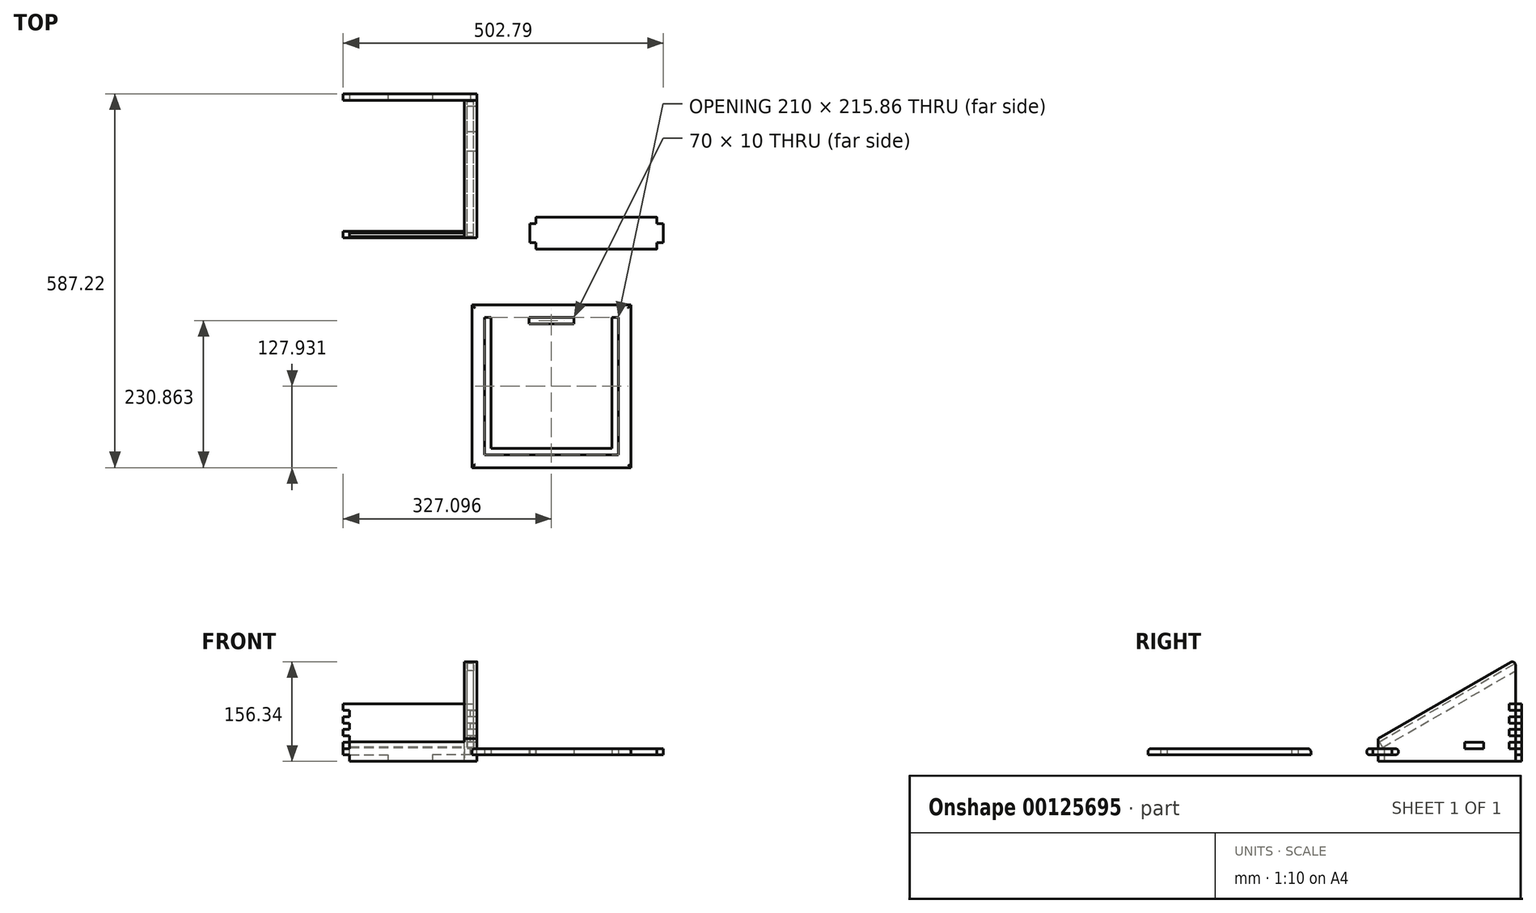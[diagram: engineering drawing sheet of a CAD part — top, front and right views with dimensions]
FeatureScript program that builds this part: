
annotation { "Feature Type Name" : "Feature", "Feature Type Description" : "" }
export const myFeature = defineFeature(function(context is Context, id is Id, definition is map)
    precondition{}
    {
        {
            var Q0;
            Q0=qCreatedBy(makeId("Right.planeOp"),FACE);
            var sketch = newSketch(context, id + "F0", { "sketchPlane" : qUnion([Q0])});
            skLineSegment(sketch, "E0", {"start": v(5, 25.39) * mm, "end": v(220.84, 150) * mm});
            skLineSegment(sketch, "E1", {"start": v(220.84, 150) * mm, "end": v(220.84, 80) * mm});
            skPoint(sketch, "E2.orphan", {"position": v(-38.97, 0) * mm});
            skLineSegment(sketch, "E3", {"start": v(-38.97, 0) * mm, "end": v(0, 22.5) * mm, "construction": true});
            skLineSegment(sketch, "E4", {"start": v(-38.97, 0) * mm, "end": v(0, 0) * mm, "construction": true});
            skLineSegment(sketch, "E5.top", {"start": v(5, -10) * mm, "end": v(220.84, -10) * mm});
            skLineSegment(sketch, "E5.right", {"start": v(220.84, 0) * mm, "end": v(220.84, -10) * mm});
            skLineSegment(sketch, "E6", {"start": v(210.84, -10) * mm, "end": v(210.84, 144.23) * mm, "construction": true});
            skLineSegment(sketch, "E7.bottom", {"start": v(220.84, 10) * mm, "end": v(210.84, 10) * mm});
            skLineSegment(sketch, "E7.top", {"start": v(220.84, 20) * mm, "end": v(210.84, 20) * mm});
            skLineSegment(sketch, "E7.right", {"start": v(210.84, 10) * mm, "end": v(210.84, 20) * mm});
            skLineSegment(sketch, "E8.bottom", {"start": v(220.84, 30) * mm, "end": v(210.84, 30) * mm});
            skLineSegment(sketch, "E8.top", {"start": v(220.84, 40) * mm, "end": v(210.84, 40) * mm});
            skLineSegment(sketch, "E8.right", {"start": v(210.84, 30) * mm, "end": v(210.84, 40) * mm});
            skLineSegment(sketch, "E9.bottom", {"start": v(220.84, 50) * mm, "end": v(210.84, 50) * mm});
            skLineSegment(sketch, "E9.top", {"start": v(220.84, 60) * mm, "end": v(210.84, 60) * mm});
            skLineSegment(sketch, "E9.right", {"start": v(210.84, 50) * mm, "end": v(210.84, 60) * mm});
            skLineSegment(sketch, "E10.trimOffspring", {"start": v(220.84, 10) * mm, "end": v(220.84, 0) * mm});
            skLineSegment(sketch, "E11.trimOffspring", {"start": v(220.84, 30) * mm, "end": v(220.84, 20) * mm});
            skLineSegment(sketch, "E12.trimOffspring", {"start": v(220.84, 50) * mm, "end": v(220.84, 40) * mm});
            skLineSegment(sketch, "E13", {"start": v(220.84, 70) * mm, "end": v(210.84, 70) * mm});
            skLineSegment(sketch, "E14", {"start": v(210.84, 70) * mm, "end": v(210.84, 80) * mm});
            skLineSegment(sketch, "E15", {"start": v(210.84, 80) * mm, "end": v(220.84, 80) * mm});
            skLineSegment(sketch, "E16.trimOffspring", {"start": v(220.84, 70) * mm, "end": v(220.84, 60) * mm});
            skLineSegment(sketch, "E17.bottom", {"start": v(170.84, 10) * mm, "end": v(140.84, 10) * mm});
            skLineSegment(sketch, "E17.top", {"start": v(170.84, 20) * mm, "end": v(140.84, 20) * mm});
            skLineSegment(sketch, "E17.left", {"start": v(170.84, 10) * mm, "end": v(170.84, 20) * mm});
            skLineSegment(sketch, "E17.right", {"start": v(140.84, 10) * mm, "end": v(140.84, 20) * mm});
            skLineSegment(sketch, "E18", {"start": v(5, -10) * mm, "end": v(5, 0) * mm});
            skLineSegment(sketch, "E19", {"start": v(0, 22.5) * mm, "end": v(5, 25.39) * mm, "construction": true});
            skLineSegment(sketch, "E20", {"start": v(5, -10) * mm, "end": v(0, -10) * mm, "construction": true});
            skLineSegment(sketch, "E21", {"start": v(0, -10) * mm, "end": v(0, 0) * mm, "construction": true});
            skLineSegment(sketch, "E22", {"start": v(0, 22.5) * mm, "end": v(0, 0) * mm, "construction": true});
            skLineSegment(sketch, "E23", {"start": v(5, 0) * mm, "end": v(15, 0) * mm});
            skLineSegment(sketch, "E24", {"start": v(15, 0) * mm, "end": v(15, 10) * mm});
            skLineSegment(sketch, "E25", {"start": v(15, 10) * mm, "end": v(5, 10) * mm});
            skLineSegment(sketch, "E26.trimOffspring", {"start": v(5, 10) * mm, "end": v(5, 25.39) * mm});
            skSolve(sketch);
        }
        {
            var Q0;
            Q0 = qSketchRegion(id + "F0", true);
            extrude(context, id + "F1", {"entities" : qUnion([Q0]), "depth" : 10 * mm});
        }
        {
            var Q0;
            Q0=makeQuery(id+"F1.opExtrude","SWEPT_EDGE",EDGE,{"disambiguationData":[OSD([sQuery(id+"F0.wireOp",EDGE,"E0"),sQuery(id+"F0.wireOp",EDGE,"E1")])]});
            cPlane(context, id + "F2", {"entities" : qUnion([Q0]), "cplaneType" : CPlaneType.LINE_ANGLE, "offset" : 25 * mm, "angle" : 330 * degree, "width" : 150 * mm, "height" : 150 * mm});
        }
        {
            var Q0;
            Q0=qCreatedBy(id+"F2.planeOp",FACE);
            var sketch = newSketch(context, id + "F3", { "sketchPlane" : qUnion([Q0])});
            skLineSegment(sketch, "E27.bottom", {"start": v(5, 14.49) * mm, "end": v(0, 14.49) * mm});
            skLineSegment(sketch, "E27.top", {"start": v(5, 3.99) * mm, "end": v(0, 3.99) * mm});
            skLineSegment(sketch, "E27.left", {"start": v(5, 14.49) * mm, "end": v(5, 3.99) * mm});
            skLineSegment(sketch, "E27.right", {"start": v(0, 14.49) * mm, "end": v(0, 3.99) * mm});
            skSolve(sketch);
        }
        {
            var Q0;
            Q0 = qSketchRegion(id + "F3", true);
            extrude(context, id + "F4", {"entities" : qUnion([Q0]), "operationType" : NewBodyOperationType.REMOVE, "depth" : 250 * mm});
        }
        {
            var Q0;
            Q0=makeQuery(id+"F1.opExtrude","SWEPT_BODY",BODY,{"disambiguationData":[OSD([sQuery(id+"F0.wireOp",EDGE,"E0"),sQuery(id+"F0.wireOp",EDGE,"E1"),sQuery(id+"F0.wireOp",EDGE,"fb4f92bf-d50f-4f46-b588-a990c1f543ed"),sQuery(id+"F0.wireOp",EDGE,"E5.top"),sQuery(id+"F0.wireOp",EDGE,"E5.left"),sQuery(id+"F0.wireOp",EDGE,"E5.right")])]});
            var Q1;
            Q1=qCreatedBy(makeId("Right.planeOp"),FACE);
            mirror(context, id + "F5", {"entities" : qUnion([Q0]), "mirrorPlane" : qUnion([Q1])});
        }
        {
            var Q0;
            Q0=qCreatedBy(makeId("Top.planeOp"),FACE);
            var sketch = newSketch(context, id + "F6", { "sketchPlane" : qUnion([Q0])});
            skLineSegment(sketch, "E28.bottom", {"start": v(2.1, -100.52) * mm, "end": v(252.1, -100.52) * mm});
            skLineSegment(sketch, "E28.top", {"start": v(2.1, -356.38) * mm, "end": v(252.1, -356.38) * mm});
            skLineSegment(sketch, "E28.left", {"start": v(2.1, -100.52) * mm, "end": v(2.1, -356.38) * mm});
            skLineSegment(sketch, "E28.right", {"start": v(252.1, -100.52) * mm, "end": v(252.1, -356.38) * mm});
            skLineSegment(sketch, "E29.0", {"start": v(232.1, -120.52) * mm, "end": v(232.1, -336.38) * mm});
            skLineSegment(sketch, "E29.2", {"start": v(22.1, -120.52) * mm, "end": v(22.1, -336.38) * mm});
            skLineSegment(sketch, "E30.0", {"start": v(222.1, -120.52) * mm, "end": v(222.1, -326.38) * mm});
            skLineSegment(sketch, "E30.2", {"start": v(32.1, -120.52) * mm, "end": v(32.1, -326.38) * mm});
            skLineSegment(sketch, "E31", {"start": v(22.1, -120.52) * mm, "end": v(32.1, -120.52) * mm});
            skLineSegment(sketch, "E32.trimOffspring", {"start": v(222.1, -120.52) * mm, "end": v(232.1, -120.52) * mm});
            skLineSegment(sketch, "E33.bottom", {"start": v(31.23, -336.38) * mm, "end": v(223, -336.38) * mm});
            skLineSegment(sketch, "E33.top", {"start": v(32.1, -326.38) * mm, "end": v(222.1, -326.38) * mm});
            skLineSegment(sketch, "E34.bottom", {"start": v(92.1, -120.52) * mm, "end": v(162.1, -120.52) * mm});
            skLineSegment(sketch, "E34.top", {"start": v(92.1, -130.52) * mm, "end": v(162.1, -130.52) * mm});
            skLineSegment(sketch, "E34.left", {"start": v(92.1, -120.52) * mm, "end": v(92.1, -130.52) * mm});
            skLineSegment(sketch, "E34.right", {"start": v(162.1, -120.52) * mm, "end": v(162.1, -130.52) * mm});
            skLineSegment(sketch, "E35", {"start": v(31.23, -336.38) * mm, "end": v(22.1, -336.38) * mm});
            skLineSegment(sketch, "E36", {"start": v(223, -336.38) * mm, "end": v(232.1, -336.38) * mm});
            skSolve(sketch);
        }
        {
            var Q0;
            Q0 = qSketchRegion(id + "F6", true);
            extrude(context, id + "F7", {"entities" : qUnion([Q0]), "depth" : 10 * mm});
        }
        {
            var Q0;
            Q0=makeQuery(id+"F1.opExtrude","CAP_FACE",FACE,{"disambiguationData":[OSD([sQuery(id+"F0.wireOp",EDGE,"E0"),sQuery(id+"F0.wireOp",EDGE,"E1"),sQuery(id+"F0.wireOp",EDGE,"fb4f92bf-d50f-4f46-b588-a990c1f543ed"),sQuery(id+"F0.wireOp",EDGE,"E5.top"),sQuery(id+"F0.wireOp",EDGE,"E5.left"),sQuery(id+"F0.wireOp",EDGE,"E5.right")])],"isStart":true});
            var sketch = newSketch(context, id + "F8", { "sketchPlane" : qUnion([Q0])});
            skLineSegment(sketch, "E37", {"start": v(-5, -10) * mm, "end": v(-15, -10) * mm});
            skLineSegment(sketch, "E38", {"start": v(-15, -10) * mm, "end": v(-15, 13.26) * mm});
            skLineSegment(sketch, "E39", {"start": v(-15, 13.26) * mm, "end": v(-12.08, 11.58) * mm});
            skLineSegment(sketch, "E40", {"start": v(-12.08, 11.58) * mm, "end": v(-6.83, 20.67) * mm});
            skLineSegment(sketch, "E41", {"start": v(-5, -10) * mm, "end": v(-5, 20.67) * mm});
            skLineSegment(sketch, "E42", {"start": v(-15, 13.26) * mm, "end": v(-15, 25.39) * mm, "construction": true});
            skLineSegment(sketch, "E43", {"start": v(-6.83, 20.67) * mm, "end": v(-5, 20.67) * mm});
            skSolve(sketch);
        }
        {
            var Q0;
            Q0 = qSketchRegion(id + "F8", true);
            extrude(context, id + "F9", {"entities" : qUnion([Q0]), "depth" : 190 * mm});
        }
        {
            var Q0;
            Q0=makeQuery(id+"F9.opExtrude","SWEPT_FACE",FACE,{"disambiguationData":[OSD([sQuery(id+"F8.wireOp",EDGE,"E41")])]});
            var sketch = newSketch(context, id + "F10", { "sketchPlane" : qUnion([Q0])});
            skLineSegment(sketch, "E44.bottom", {"start": v(0, 0) * mm, "end": v(10, 0) * mm});
            skLineSegment(sketch, "E44.top", {"start": v(0, 10) * mm, "end": v(10, 10) * mm});
            skLineSegment(sketch, "E44.left", {"start": v(0, 0) * mm, "end": v(0, 10) * mm});
            skLineSegment(sketch, "E44.right", {"start": v(10, 0) * mm, "end": v(10, 10) * mm});
            skLineSegment(sketch, "E45.bottom", {"start": v(-190, 0) * mm, "end": v(-200, 0) * mm});
            skLineSegment(sketch, "E45.top", {"start": v(-190, 10) * mm, "end": v(-200, 10) * mm});
            skLineSegment(sketch, "E45.left", {"start": v(-190, 0) * mm, "end": v(-190, 10) * mm});
            skLineSegment(sketch, "E45.right", {"start": v(-200, 0) * mm, "end": v(-200, 10) * mm});
            skSolve(sketch);
        }
        {
            var Q0;
            Q0 = qSketchRegion(id + "F10", true);
            extrude(context, id + "F11", {"entities" : qUnion([Q0]), "operationType" : NewBodyOperationType.ADD, "oppositeDirection" : true, "depth" : 10 * mm});
        }
        {
            var Q0;
            Q0=makeQuery(id+"F1.opExtrude","SWEPT_FACE",FACE,{"disambiguationData":[OSD([sQuery(id+"F0.wireOp",EDGE,"E5.right"),sQuery(id+"F0.wireOp",EDGE,"E10.trimOffspring")])]});
            var sketch = newSketch(context, id + "F12", { "sketchPlane" : qUnion([Q0])});
            skLineSegment(sketch, "E46", {"start": v(0, 0) * mm, "end": v(0, 10) * mm});
            skLineSegment(sketch, "E47", {"start": v(0, 10) * mm, "end": v(-10, 10) * mm});
            skLineSegment(sketch, "E48", {"start": v(-10, 10) * mm, "end": v(-10, 20) * mm});
            skLineSegment(sketch, "E49", {"start": v(-10, 20) * mm, "end": v(0, 20) * mm});
            skLineSegment(sketch, "E50", {"start": v(0, 20) * mm, "end": v(0, 30) * mm});
            skLineSegment(sketch, "E51", {"start": v(0, 30) * mm, "end": v(-10, 30) * mm});
            skLineSegment(sketch, "E52", {"start": v(-10, 30) * mm, "end": v(-10, 40) * mm});
            skLineSegment(sketch, "E53", {"start": v(-10, 40) * mm, "end": v(0, 40) * mm});
            skLineSegment(sketch, "E54", {"start": v(0, 40) * mm, "end": v(0, 50) * mm});
            skLineSegment(sketch, "E55", {"start": v(0, 50) * mm, "end": v(-10, 50) * mm});
            skLineSegment(sketch, "E56", {"start": v(-10, 50) * mm, "end": v(-10, 60) * mm});
            skLineSegment(sketch, "E57", {"start": v(-10, 60) * mm, "end": v(0, 60) * mm});
            skLineSegment(sketch, "E58", {"start": v(95, -10) * mm, "end": v(95, 115.91) * mm, "construction": true});
            skLineSegment(sketch, "E59", {"start": v(0, 0) * mm, "end": v(60, 0) * mm});
            skLineSegment(sketch, "E60", {"start": v(60, 0) * mm, "end": v(60, -10) * mm});
            skLineSegment(sketch, "E61", {"start": v(60, -10) * mm, "end": v(95, -10) * mm});
            skLineSegment(sketch, "E62.MirrorCS", {"start": v(190, 50) * mm, "end": v(200, 50) * mm});
            skLineSegment(sketch, "E63.MirrorCS", {"start": v(190, 40) * mm, "end": v(190, 50) * mm});
            skLineSegment(sketch, "E64.MirrorCS", {"start": v(200, 50) * mm, "end": v(200, 60) * mm});
            skLineSegment(sketch, "E65.MirrorCS", {"start": v(200, 40) * mm, "end": v(190, 40) * mm});
            skLineSegment(sketch, "E66.MirrorCS", {"start": v(200, 60) * mm, "end": v(190, 60) * mm});
            skLineSegment(sketch, "E67.MirrorCS", {"start": v(200, 30) * mm, "end": v(200, 40) * mm});
            skLineSegment(sketch, "E68.MirrorCS", {"start": v(190, 30) * mm, "end": v(200, 30) * mm});
            skLineSegment(sketch, "E69.MirrorCS", {"start": v(190, 20) * mm, "end": v(190, 30) * mm});
            skLineSegment(sketch, "E70.MirrorCS", {"start": v(200, 20) * mm, "end": v(190, 20) * mm});
            skLineSegment(sketch, "E71.MirrorCS", {"start": v(190, 10) * mm, "end": v(200, 10) * mm});
            skLineSegment(sketch, "E72.MirrorCS", {"start": v(200, 10) * mm, "end": v(200, 20) * mm});
            skLineSegment(sketch, "E73.MirrorCS", {"start": v(190, 0) * mm, "end": v(190, 10) * mm});
            skLineSegment(sketch, "E74.MirrorCS", {"start": v(190, 0) * mm, "end": v(130, 0) * mm});
            skLineSegment(sketch, "E75.MirrorCS", {"start": v(130, 0) * mm, "end": v(130, -10) * mm});
            skLineSegment(sketch, "E76.MirrorCS", {"start": v(130, -10) * mm, "end": v(95, -10) * mm});
            skLineSegment(sketch, "E77", {"start": v(0, 60) * mm, "end": v(0, 70) * mm});
            skLineSegment(sketch, "E78", {"start": v(0, 70) * mm, "end": v(-10, 70) * mm});
            skLineSegment(sketch, "E79", {"start": v(-10, 80) * mm, "end": v(95, 80) * mm});
            skLineSegment(sketch, "E80", {"start": v(-10, 70) * mm, "end": v(-10, 80) * mm});
            skPoint(sketch, "E81.end.orphan", {"position": v(95, 60) * mm});
            skPoint(sketch, "E82.MirrorCS.start.orphan", {"position": v(190, 60) * mm});
            skLineSegment(sketch, "E83.MirrorCS", {"start": v(200, 80) * mm, "end": v(95, 80) * mm});
            skLineSegment(sketch, "E84.MirrorCS", {"start": v(200, 70) * mm, "end": v(200, 80) * mm});
            skLineSegment(sketch, "E85.MirrorCS", {"start": v(190, 70) * mm, "end": v(200, 70) * mm});
            skLineSegment(sketch, "E86.MirrorCS", {"start": v(190, 60) * mm, "end": v(190, 70) * mm});
            skSolve(sketch);
        }
        {
            var Q0;
            Q0 = qSketchRegion(id + "F12", true);
            extrude(context, id + "F13", {"entities" : qUnion([Q0]), "depth" : 10 * mm});
        }
        {
            var Q0;
            Q0=qCreatedBy(makeId("Top.planeOp"),FACE);
            var sketch = newSketch(context, id + "F14", { "sketchPlane" : qUnion([Q0])});
            skLineSegment(sketch, "E87.bottom", {"start": v(102.79, 37.09) * mm, "end": v(292.79, 37.09) * mm});
            skLineSegment(sketch, "E87.top", {"start": v(102.79, -12.91) * mm, "end": v(292.79, -12.91) * mm});
            skLineSegment(sketch, "E87.left", {"start": v(102.79, 37.09) * mm, "end": v(102.79, 27.09) * mm});
            skLineSegment(sketch, "E87.right", {"start": v(292.79, 37.09) * mm, "end": v(292.79, 27.09) * mm});
            skLineSegment(sketch, "E88.bottom", {"start": v(292.79, 27.09) * mm, "end": v(302.79, 27.09) * mm});
            skLineSegment(sketch, "E88.top", {"start": v(292.79, -2.91) * mm, "end": v(302.79, -2.91) * mm});
            skLineSegment(sketch, "E88.right", {"start": v(302.79, 27.09) * mm, "end": v(302.79, -2.91) * mm});
            skLineSegment(sketch, "E89.bottom", {"start": v(102.79, -2.91) * mm, "end": v(92.79, -2.91) * mm});
            skLineSegment(sketch, "E89.top", {"start": v(102.79, 27.09) * mm, "end": v(92.79, 27.09) * mm});
            skLineSegment(sketch, "E89.right", {"start": v(92.79, -2.91) * mm, "end": v(92.79, 27.09) * mm});
            skLineSegment(sketch, "E90.trimOffspring", {"start": v(102.79, -2.91) * mm, "end": v(102.79, -12.91) * mm});
            skLineSegment(sketch, "E91.trimOffspring", {"start": v(292.79, -2.91) * mm, "end": v(292.79, -12.91) * mm});
            skSolve(sketch);
        }
        {
            var Q0;
            Q0 = qSketchRegion(id + "F14", true);
            extrude(context, id + "F15", {"entities" : qUnion([Q0]), "depth" : 10 * mm});
        }
        {
            var Q0;
            Q0=makeQuery(id+"F5.opPattern","COPY",EDGE,{"derivedFrom":makeQuery(id+"F1.opExtrude","SWEPT_EDGE",EDGE,{"disambiguationData":[OSD([sQuery(id+"F0.wireOp",EDGE,"E0"),sQuery(id+"F0.wireOp",EDGE,"E1")])]}),"instanceName":"1"});
            var Q1;
            Q1=makeQuery(id+"F1.opExtrude","SWEPT_EDGE",EDGE,{"disambiguationData":[OSD([sQuery(id+"F0.wireOp",EDGE,"E0"),sQuery(id+"F0.wireOp",EDGE,"E1")])]});
            fillet(context, id + "F16", {"entities" : qUnion([Q0, Q1]), "radius" : 5 * mm, "tangentPropagation" : true, "allowEdgeOverflow" : false});
        }
        {
            var Q0;
            Q0=makeQuery(id+"F7.opExtrude","CAP_EDGE",EDGE,{"disambiguationData":[OSD([sQuery(id+"F6.wireOp",EDGE,"E28.left")])],"isStart":false});
            var Q1;
            Q1=makeQuery(id+"F7.opExtrude","CAP_EDGE",EDGE,{"disambiguationData":[OSD([sQuery(id+"F6.wireOp",EDGE,"E28.top")])],"isStart":false});
            var Q2;
            Q2=makeQuery(id+"F7.opExtrude","CAP_EDGE",EDGE,{"disambiguationData":[OSD([sQuery(id+"F6.wireOp",EDGE,"E28.right")])],"isStart":false});
            var Q3;
            Q3=makeQuery(id+"F7.opExtrude","CAP_EDGE",EDGE,{"disambiguationData":[OSD([sQuery(id+"F6.wireOp",EDGE,"E28.bottom")])],"isStart":false});
            fillet(context, id + "F17", {"entities" : qUnion([Q0, Q1, Q2, Q3]), "radius" : 5 * mm, "tangentPropagation" : true, "allowEdgeOverflow" : false});
        }
        {
            var Q0;
            Q0=makeQuery(id+"F15.opExtrude","CAP_EDGE",EDGE,{"disambiguationData":[OSD([sQuery(id+"F14.wireOp",EDGE,"E87.bottom")])],"isStart":false});
            var Q1;
            Q1=makeQuery(id+"F15.opExtrude","CAP_EDGE",EDGE,{"disambiguationData":[OSD([sQuery(id+"F14.wireOp",EDGE,"E87.bottom")])],"isStart":true});
            var Q2;
            Q2=makeQuery(id+"F15.opExtrude","CAP_EDGE",EDGE,{"disambiguationData":[OSD([sQuery(id+"F14.wireOp",EDGE,"E87.top")])],"isStart":false});
            var Q3;
            Q3=makeQuery(id+"F15.opExtrude","CAP_EDGE",EDGE,{"disambiguationData":[OSD([sQuery(id+"F14.wireOp",EDGE,"E87.top")])],"isStart":true});
            fillet(context, id + "F18", {"entities" : qUnion([Q0, Q1, Q2, Q3]), "radius" : 5 * mm, "tangentPropagation" : true, "allowEdgeOverflow" : false});
        }
    });
